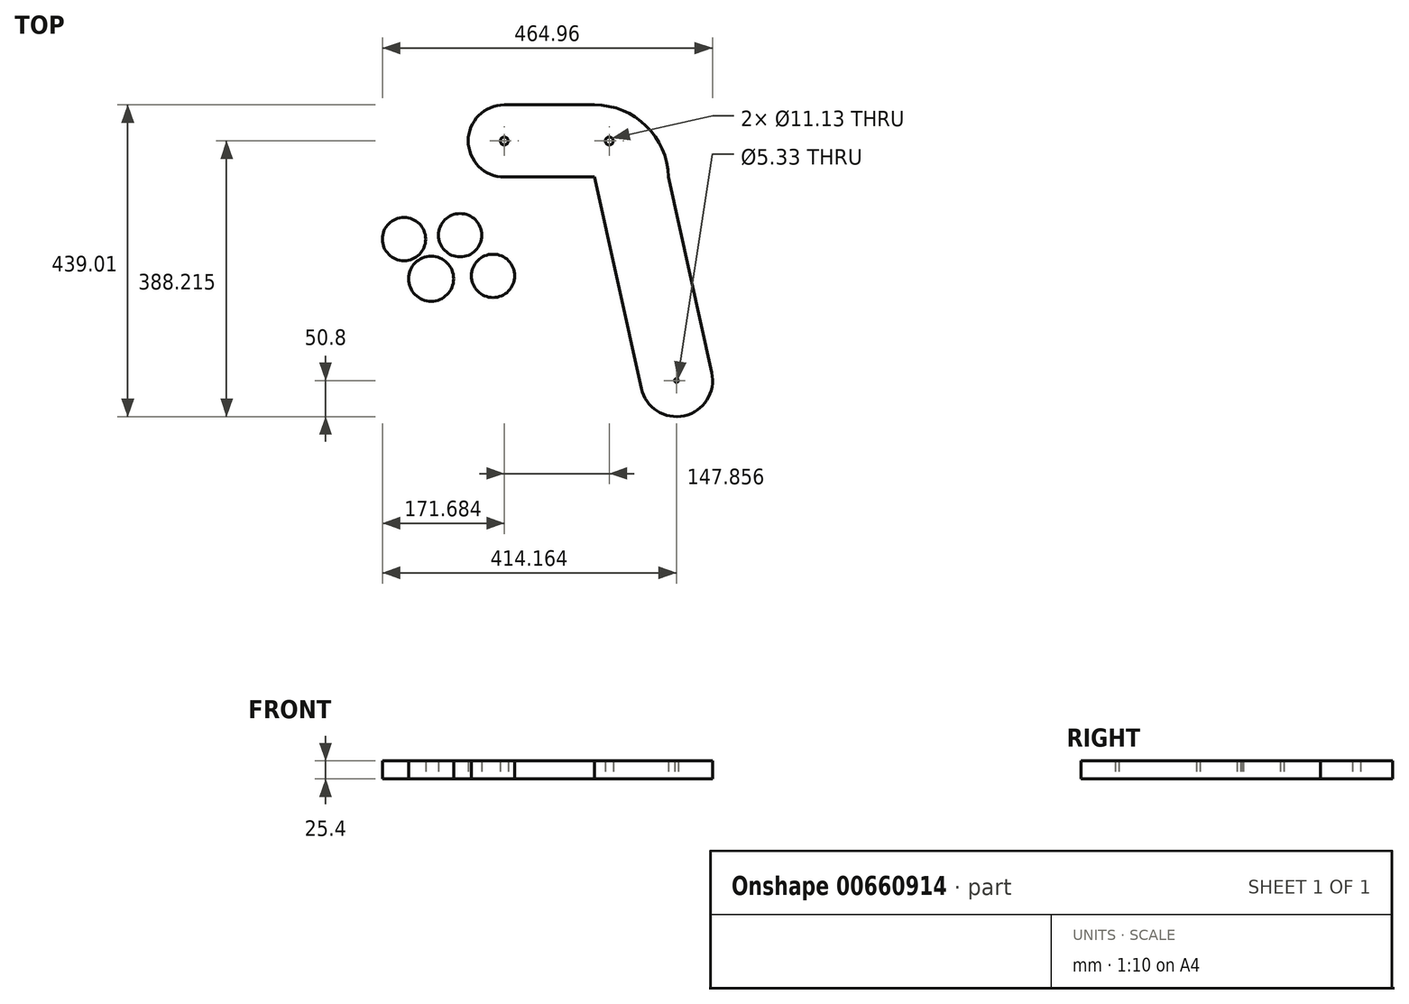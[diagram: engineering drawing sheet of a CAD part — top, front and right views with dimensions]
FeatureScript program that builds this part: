
annotation { "Feature Type Name" : "Feature", "Feature Type Description" : "" }
export const myFeature = defineFeature(function(context is Context, id is Id, definition is map)
    precondition{}
    {
        {
            var Q0;
            Q0=qCreatedBy(makeId("Top.planeOp"),FACE);
            var sketch = newSketch(context, id + "F0", { "sketchPlane" : qUnion([Q0])});
            skLineSegment(sketch, "E0", {"start": v(-20.86, -58.45) * mm, "end": v(45.03, -356.04) * mm});
            skLineSegment(sketch, "E1", {"start": v(144.22, -334.08) * mm, "end": v(83.2, -58.45) * mm});
            skArc(sketch, "E2", {"start": v(83.2, -58.45) * mm, "mid": v(51.86, 13.54) * mm, "end": v(-20.86, 43.15) * mm});
            skArc(sketch, "E3", {"start": v(45.03, -356.04) * mm, "mid": v(105.6, -394.66) * mm, "end": v(144.22, -334.08) * mm});
            skCircle(sketch, "E4", {"center": v(94.62, -345.06) * mm, "radius": 2.67 * mm});
            skCircle(sketch, "E5", {"center": v(-289.06, -145.83) * mm, "radius": 30.48 * mm});
            skCircle(sketch, "E6", {"center": v(-210, -140.37) * mm, "radius": 30.48 * mm});
            skCircle(sketch, "E7", {"center": v(-250.89, -201.71) * mm, "radius": 31.7 * mm});
            skCircle(sketch, "E8", {"center": v(-163.65, -197.63) * mm, "radius": 30.48 * mm});
            skLineSegment(sketch, "E9", {"start": v(-20.86, 43.15) * mm, "end": v(-147.86, 43.15) * mm});
            skLineSegment(sketch, "E10", {"start": v(-20.86, -58.45) * mm, "end": v(-147.86, -58.45) * mm});
            skArc(sketch, "E11", {"start": v(-147.86, 43.15) * mm, "mid": v(-198.66, -7.65) * mm, "end": v(-147.86, -58.45) * mm});
            skCircle(sketch, "E12", {"center": v(-147.86, -7.65) * mm, "radius": 5.56 * mm});
            skCircle(sketch, "E13", {"center": v(0, -7.65) * mm, "radius": 5.56 * mm});
            skSolve(sketch);
        }
        {
            var Q0;
            Q0=makeQuery(id+"F0.imprint","IMPRINT",FACE,{"disambiguationData":[TD([[makeQuery(id+"F0.imprint","IMPRINT",EDGE,{"derivedFrom":sQuery(id+"F0.wireOp",EDGE,"0O9jmoRn-VUxU-qZSm-5AKD-WEZJ4WSUoZFV.bottom")}),-1.0]])]});
            var Q1;
            Q1=makeQuery(id+"F0.imprint","IMPRINT",FACE,{"disambiguationData":[TD([[makeQuery(id+"F0.imprint","IMPRINT",EDGE,{"derivedFrom":sQuery(id+"F0.wireOp",EDGE,"E6")}),1.0]])]});
            var Q2;
            Q2=makeQuery(id+"F0.imprint","IMPRINT",FACE,{"disambiguationData":[TD([[makeQuery(id+"F0.imprint","IMPRINT",EDGE,{"derivedFrom":sQuery(id+"F0.wireOp",EDGE,"E8")}),1.0]])]});
            var Q3;
            Q3=makeQuery(id+"F0.imprint","IMPRINT",FACE,{"disambiguationData":[TD([[makeQuery(id+"F0.imprint","IMPRINT",EDGE,{"derivedFrom":sQuery(id+"F0.wireOp",EDGE,"E7")}),1.0]])]});
            var Q4;
            Q4=makeQuery(id+"F0.imprint","IMPRINT",FACE,{"disambiguationData":[TD([[makeQuery(id+"F0.imprint","IMPRINT",EDGE,{"derivedFrom":sQuery(id+"F0.wireOp",EDGE,"E5")}),1.0]])]});
            var Q5;
            Q5=makeQuery(id+"F0.imprint","IMPRINT",FACE,{"disambiguationData":[TD([[makeQuery(id+"F0.imprint","IMPRINT",EDGE,{"derivedFrom":sQuery(id+"F0.wireOp",EDGE,"E0")}),1.0]])]});
            extrude(context, id + "F1", {"entities" : qUnion([Q0, Q1, Q2, Q3, Q4, Q5]), "depth" : 25.4 * mm, "offsetDistance" : 25.4 * mm});
        }
    });
